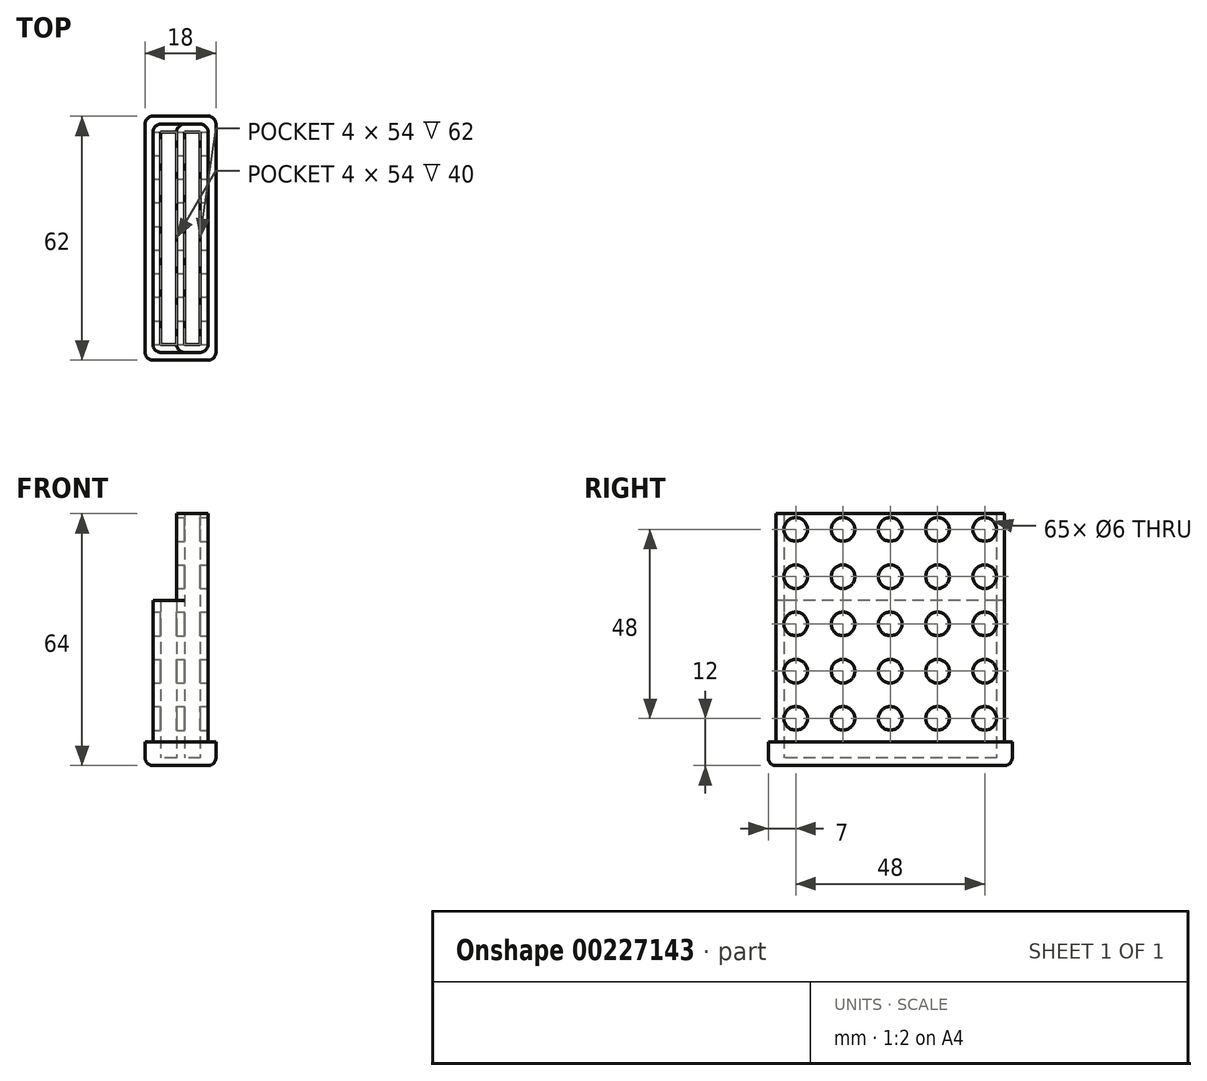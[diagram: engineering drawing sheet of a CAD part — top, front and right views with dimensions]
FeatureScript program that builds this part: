
annotation { "Feature Type Name" : "Feature", "Feature Type Description" : "" }
export const myFeature = defineFeature(function(context is Context, id is Id, definition is map)
    precondition{}
    {
        {
            var Q0;
            Q0=qCreatedBy(makeId("Top.planeOp"),FACE);
            var sketch = newSketch(context, id + "F0", { "sketchPlane" : qUnion([Q0])});
            skLineSegment(sketch, "E0.bottom", {"start": v(4, 29) * mm, "end": v(-4, 29) * mm});
            skLineSegment(sketch, "E0.top", {"start": v(4, -29) * mm, "end": v(-4, -29) * mm});
            skLineSegment(sketch, "E0.left", {"start": v(4, 29) * mm, "end": v(4, -29) * mm});
            skLineSegment(sketch, "E0.right", {"start": v(-4, 29) * mm, "end": v(-4, -29) * mm});
            skPoint(sketch, "E0.middle", {"position": v(0, 0) * mm});
            skLineSegment(sketch, "E1.bottom", {"start": v(2, 27) * mm, "end": v(-2, 27) * mm});
            skLineSegment(sketch, "E1.top", {"start": v(2, -27) * mm, "end": v(-2, -27) * mm});
            skLineSegment(sketch, "E1.left", {"start": v(2, 27) * mm, "end": v(2, -27) * mm});
            skLineSegment(sketch, "E1.right", {"start": v(-2, 27) * mm, "end": v(-2, -27) * mm});
            skLineSegment(sketch, "E2", {"start": v(-10, 27) * mm, "end": v(-10, -27) * mm});
            skLineSegment(sketch, "E3", {"start": v(-4, 27) * mm, "end": v(-8, 27) * mm});
            skLineSegment(sketch, "E4", {"start": v(-8, 27) * mm, "end": v(-8, -27) * mm});
            skLineSegment(sketch, "E5", {"start": v(-8, -27) * mm, "end": v(-4, -27) * mm});
            skLineSegment(sketch, "E6", {"start": v(-4, -29) * mm, "end": v(-10, -29) * mm});
            skLineSegment(sketch, "E7", {"start": v(-10, -29) * mm, "end": v(-10, -27) * mm});
            skLineSegment(sketch, "E8", {"start": v(-4, 29) * mm, "end": v(-10, 29) * mm});
            skLineSegment(sketch, "E9", {"start": v(-10, 29) * mm, "end": v(-10, 27) * mm});
            skSolve(sketch);
        }
        {
            var Q0;
            {var subQ0=sQuery(id+"F0.wireOp",EDGE,"E1.right");Q0=makeQuery(id+"F0.imprint","IMPRINT",FACE,{"disambiguationData":[TD([[makeQuery(id+"F0.imprint","IMPRINT",EDGE,{"derivedFrom":subQ0}),-1.0]])]});}
            var Q1;
            {var subQ2=sQuery(id+"F0.wireOp",EDGE,"E0.top");Q1=makeQuery(id+"F0.imprint","IMPRINT",FACE,{"disambiguationData":[TD([[makeQuery(id+"F0.imprint","IMPRINT",EDGE,{"derivedFrom":subQ2}),-1.0]])]});}
            var Q2;
            {var subQ2=sQuery(id+"F0.wireOp",EDGE,"E0.bottom");Q2=makeQuery(id+"F0.imprint","IMPRINT",FACE,{"disambiguationData":[TD([[makeQuery(id+"F0.imprint","IMPRINT",EDGE,{"derivedFrom":subQ2}),1.0]])]});}
            var Q3;
            {var subQ0=sQuery(id+"F0.wireOp",EDGE,"E1.left");Q3=makeQuery(id+"F0.imprint","IMPRINT",FACE,{"disambiguationData":[TD([[makeQuery(id+"F0.imprint","IMPRINT",EDGE,{"derivedFrom":subQ0}),1.0]])]});}
            extrude(context, id + "F1", {"entities" : qUnion([Q0, Q1, Q2, Q3]), "depth" : 62 * mm});
        }
        {
            var Q0;
            {var subQ0=sQuery(id+"F0.wireOp",EDGE,"E2");Q0=makeQuery(id+"F0.imprint","IMPRINT",FACE,{"disambiguationData":[TD([[makeQuery(id+"F0.imprint","IMPRINT",EDGE,{"derivedFrom":subQ0}),1.0]])]});}
            extrude(context, id + "F2", {"entities" : qUnion([Q0]), "operationType" : NewBodyOperationType.ADD, "depth" : 40 * mm});
        }
        {
            var Q0;
            Q0=makeQuery(id+"F2.opExtrude","SWEPT_EDGE",EDGE,{"disambiguationData":[OSD([sQuery(id+"F0.wireOp",EDGE,"E6"),sQuery(id+"F0.wireOp",EDGE,"E7")])]});
            var Q1;
            Q1=makeQuery(id+"F2.opExtrude","SWEPT_EDGE",EDGE,{"disambiguationData":[OSD([sQuery(id+"F0.wireOp",EDGE,"E8"),sQuery(id+"F0.wireOp",EDGE,"E9")])]});
            var Q2;
            Q2=makeQuery(id+"F1.opExtrude","SWEPT_EDGE",EDGE,{"disambiguationData":[OSD([sQuery(id+"F0.wireOp",EDGE,"E0.top"),sQuery(id+"F0.wireOp",EDGE,"E0.right"),sQuery(id+"F0.wireOp",EDGE,"E6")])]});
            var Q3;
            Q3=makeQuery(id+"F1.opExtrude","SWEPT_EDGE",EDGE,{"disambiguationData":[OSD([sQuery(id+"F0.wireOp",EDGE,"E0.bottom"),sQuery(id+"F0.wireOp",EDGE,"E0.right"),sQuery(id+"F0.wireOp",EDGE,"E8")])]});
            fillet(context, id + "F3", {"entities" : qUnion([Q0, Q1, Q2, Q3]), "radius" : 2 * mm, "tangentPropagation" : true, "allowEdgeOverflow" : false});
        }
        {
            var Q0;
            Q0=makeQuery(id+"F1.opExtrude","SWEPT_EDGE",EDGE,{"disambiguationData":[OSD([sQuery(id+"F0.wireOp",EDGE,"E0.top"),sQuery(id+"F0.wireOp",EDGE,"E0.left")])]});
            var Q1;
            Q1=makeQuery(id+"F1.opExtrude","SWEPT_EDGE",EDGE,{"disambiguationData":[OSD([sQuery(id+"F0.wireOp",EDGE,"E0.bottom"),sQuery(id+"F0.wireOp",EDGE,"E0.left")])]});
            fillet(context, id + "F4", {"entities" : qUnion([Q0, Q1]), "radius" : 2 * mm, "tangentPropagation" : true, "allowEdgeOverflow" : false});
        }
        {
            var Q0;
            Q0=makeQuery(id+"F1.opExtrude","SWEPT_FACE",FACE,{"disambiguationData":[OSD([sQuery(id+"F0.wireOp",EDGE,"E0.left")])]});
            var sketch = newSketch(context, id + "F5", { "sketchPlane" : qUnion([Q0])});
            skCircle(sketch, "E10", {"center": v(-24, 10) * mm, "radius": 3 * mm});
            skCircle(sketch, "E11.0.1.0", {"center": v(-24, 22) * mm, "radius": 3 * mm});
            skCircle(sketch, "E11.0.2.0", {"center": v(-24, 34) * mm, "radius": 3 * mm});
            skCircle(sketch, "E11.0.3.0", {"center": v(-24, 46) * mm, "radius": 3 * mm});
            skCircle(sketch, "E11.1.0.0", {"center": v(-12, 10) * mm, "radius": 3 * mm});
            skCircle(sketch, "E11.1.1.0", {"center": v(-12, 22) * mm, "radius": 3 * mm});
            skCircle(sketch, "E11.1.2.0", {"center": v(-12, 34) * mm, "radius": 3 * mm});
            skCircle(sketch, "E11.1.3.0", {"center": v(-12, 46) * mm, "radius": 3 * mm});
            skCircle(sketch, "E11.2.0.0", {"center": v(0, 10) * mm, "radius": 3 * mm});
            skCircle(sketch, "E11.2.1.0", {"center": v(0, 22) * mm, "radius": 3 * mm});
            skCircle(sketch, "E11.2.2.0", {"center": v(0, 34) * mm, "radius": 3 * mm});
            skCircle(sketch, "E11.2.3.0", {"center": v(0, 46) * mm, "radius": 3 * mm});
            skCircle(sketch, "E11.3.0.0", {"center": v(12, 10) * mm, "radius": 3 * mm});
            skCircle(sketch, "E11.3.1.0", {"center": v(12, 22) * mm, "radius": 3 * mm});
            skCircle(sketch, "E11.3.2.0", {"center": v(12, 34) * mm, "radius": 3 * mm});
            skCircle(sketch, "E11.3.3.0", {"center": v(12, 46) * mm, "radius": 3 * mm});
            skCircle(sketch, "E11.4.0.0", {"center": v(24, 10) * mm, "radius": 3 * mm});
            skCircle(sketch, "E11.4.1.0", {"center": v(24, 22) * mm, "radius": 3 * mm});
            skCircle(sketch, "E11.4.2.0", {"center": v(24, 34) * mm, "radius": 3 * mm});
            skCircle(sketch, "E11.4.3.0", {"center": v(24, 46) * mm, "radius": 3 * mm});
            skLineSegment(sketch, "E11.direction1", {"start": v(-24, 10) * mm, "end": v(-12, 10) * mm, "construction": true});
            skLineSegment(sketch, "E11.direction2", {"start": v(-24, 10) * mm, "end": v(-24, 22) * mm, "construction": true});
            skCircle(sketch, "E12.0.0.4", {"center": v(-24, 58) * mm, "radius": 3 * mm});
            skCircle(sketch, "E12.0.1.4", {"center": v(-12, 58) * mm, "radius": 3 * mm});
            skCircle(sketch, "E12.0.2.4", {"center": v(0, 58) * mm, "radius": 3 * mm});
            skCircle(sketch, "E12.0.3.4", {"center": v(12, 58) * mm, "radius": 3 * mm});
            skCircle(sketch, "E12.0.4.4", {"center": v(24, 58) * mm, "radius": 3 * mm});
            skSolve(sketch);
        }
        {
            var Q0;
            Q0 = qSketchRegion(id + "F5", true);
            extrude(context, id + "F6", {"entities" : qUnion([Q0]), "operationType" : NewBodyOperationType.REMOVE, "endBound" : BoundingType.THROUGH_ALL, "oppositeDirection" : true, "depth" : 25 * mm});
        }
        {
            var Q0;
            {var subQ1=sQuery(id+"F0.wireOp",EDGE,"E0.bottom");Q0=makeQuery(id+"F0.imprint","IMPRINT",FACE,{"disambiguationData":[TD([[makeQuery(id+"F0.imprint","IMPRINT",EDGE,{"derivedFrom":subQ1}),1.0]])]});}
            var sketch = newSketch(context, id + "F7", { "sketchPlane" : qUnion([Q0])});
            skLineSegment(sketch, "E13", {"start": v(6, -29) * mm, "end": v(6, 29) * mm});
            skLineSegment(sketch, "E14", {"start": v(4, 31) * mm, "end": v(-10, 31) * mm});
            skLineSegment(sketch, "E15", {"start": v(-12, 29) * mm, "end": v(-12, -29) * mm});
            skLineSegment(sketch, "E16", {"start": v(-10, -31) * mm, "end": v(4, -31) * mm});
            skPoint(sketch, "E17.visualSharp", {"position": v(6, -31) * mm});
            skArc(sketch, "E17.filletArc", {"start": v(4, -31) * mm, "mid": v(5.41, -30.41) * mm, "end": v(6, -29) * mm});
            skPoint(sketch, "E18.visualSharp", {"position": v(-12, -31) * mm});
            skArc(sketch, "E18.filletArc", {"start": v(-12, -29) * mm, "mid": v(-11.41, -30.41) * mm, "end": v(-10, -31) * mm});
            skPoint(sketch, "E19.visualSharp", {"position": v(-12, 31) * mm});
            skArc(sketch, "E19.filletArc", {"start": v(-10, 31) * mm, "mid": v(-11.41, 30.41) * mm, "end": v(-12, 29) * mm});
            skPoint(sketch, "E20.visualSharp", {"position": v(6, 31) * mm});
            skArc(sketch, "E20.filletArc", {"start": v(6, 29) * mm, "mid": v(5.41, 30.41) * mm, "end": v(4, 31) * mm});
            skSolve(sketch);
        }
        {
            var Q0;
            Q0 = qSketchRegion(id + "F7", true);
            extrude(context, id + "F8", {"entities" : qUnion([Q0]), "operationType" : NewBodyOperationType.ADD, "oppositeDirection" : true, "depth" : 2 * mm});
        }
        {
            var Q0;
            {var subQ1=sQuery(id+"F0.wireOp",EDGE,"E0.bottom");var subQ4=sQuery(id+"F7.wireOp",EDGE,"E19.filletArc");var subQ6=sQuery(id+"F7.wireOp",EDGE,"E16");var subQ9=sQuery(id+"F7.wireOp",EDGE,"E15");var subQ10=sQuery(id+"F7.wireOp",EDGE,"E13");var subQ11=sQuery(id+"F7.wireOp",EDGE,"E14");var subQ12=sQuery(id+"F7.wireOp",EDGE,"E17.filletArc");var subQ13=sQuery(id+"F7.wireOp",EDGE,"E18.filletArc");var subQ14=sQuery(id+"F7.wireOp",EDGE,"E20.filletArc");Q0=makeQuery(id+"F8.boolean.opBoolean","SPLIT",FACE,{"disambiguationData":[TD([makeQuery(id+"F1.opExtrude","SWEPT_FACE",FACE,{"disambiguationData":[OSD([subQ1])]})])],"derivedFrom":makeQuery(id+"F8.opExtrude","CAP_FACE",FACE,{"disambiguationData":[OSD([subQ10,subQ11,subQ9,subQ6,subQ12,subQ13,subQ4,subQ14])],"isStart":true})});}
            extrude(context, id + "F9", {"entities" : qUnion([Q0]), "operationType" : NewBodyOperationType.ADD, "depth" : 4 * mm});
        }
        {
            var Q0;
            Q0=makeQuery(id+"F8.opExtrude","CAP_EDGE",EDGE,{"disambiguationData":[OSD([sQuery(id+"F7.wireOp",EDGE,"E13")])],"isStart":false});
            fillet(context, id + "F10", {"entities" : qUnion([Q0]), "radius" : 2 * mm, "tangentPropagation" : true, "allowEdgeOverflow" : false});
        }
    });
